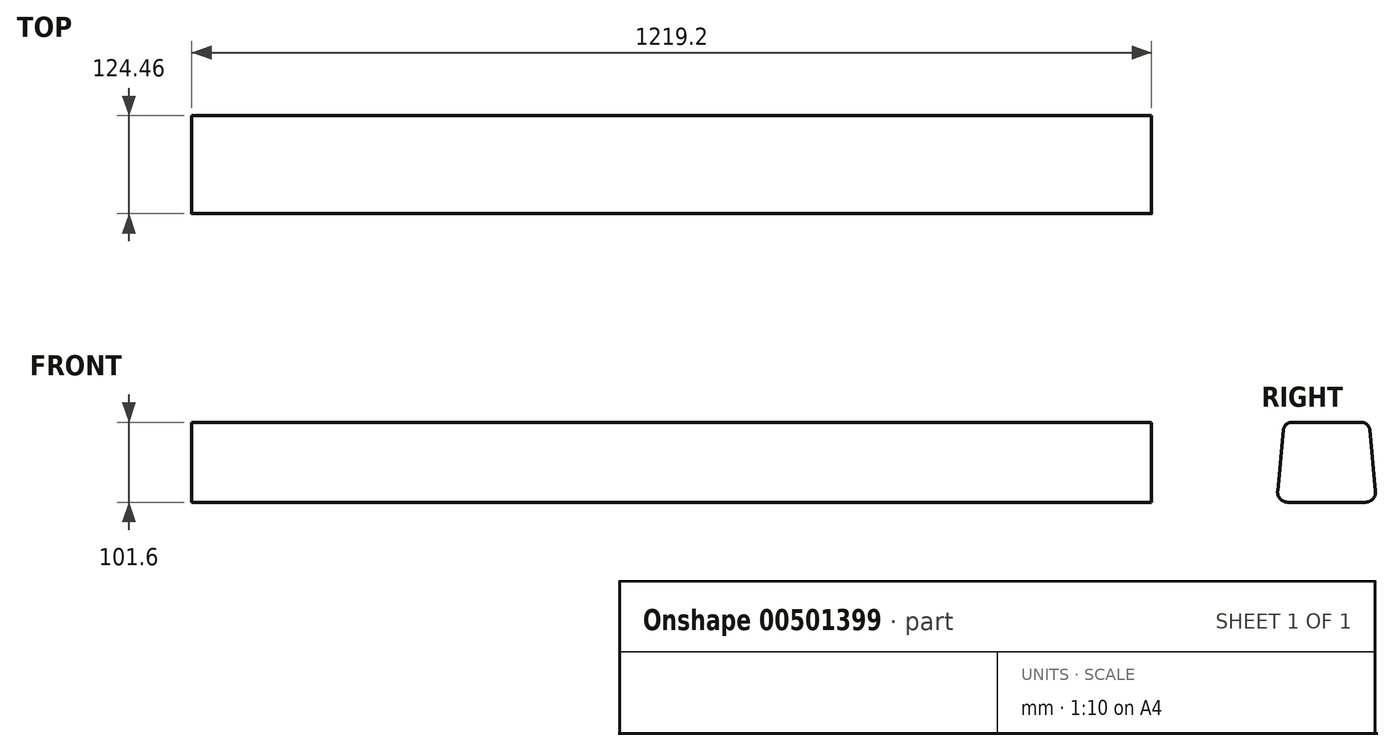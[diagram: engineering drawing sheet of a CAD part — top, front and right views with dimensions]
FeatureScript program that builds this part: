
annotation { "Feature Type Name" : "Feature", "Feature Type Description" : "" }
export const myFeature = defineFeature(function(context is Context, id is Id, definition is map)
    precondition{}
    {
        {
            var Q0;
            Q0=qCreatedBy(makeId("Top.planeOp"),FACE);
            var sketch = newSketch(context, id + "F0", { "sketchPlane" : qUnion([Q0])});
            skLineSegment(sketch, "E0.bottom", {"start": v(0, 0) * mm, "end": v(1219.2, 0) * mm});
            skLineSegment(sketch, "E0.top", {"start": v(0, 127) * mm, "end": v(1219.2, 127) * mm});
            skLineSegment(sketch, "E0.left", {"start": v(0, 0) * mm, "end": v(0, 127) * mm});
            skLineSegment(sketch, "E0.right", {"start": v(1219.2, 0) * mm, "end": v(1219.2, 127) * mm});
            skSolve(sketch);
        }
        {
            var Q0;
            Q0 = qSketchRegion(id + "F0", true);
            extrude(context, id + "F1", {"entities" : qUnion([Q0]), "depth" : 101.6 * mm});
        }
        {
            var Q0;
            Q0=makeQuery(id+"F1.opExtrude","SWEPT_FACE",FACE,{"disambiguationData":[OSD([sQuery(id+"F0.wireOp",EDGE,"E0.right")])]});
            var sketch = newSketch(context, id + "F2", { "sketchPlane" : qUnion([Q0])});
            skLineSegment(sketch, "E1", {"start": v(0, 101.6) * mm, "end": v(9.58, 101.6) * mm});
            skLineSegment(sketch, "E2", {"start": v(0, 101.6) * mm, "end": v(0, 0) * mm});
            skLineSegment(sketch, "E3", {"start": v(0, 0) * mm, "end": v(7.05, 0) * mm});
            skLineSegment(sketch, "E4", {"start": v(8.66, 91.9) * mm, "end": v(1.33, 14.1) * mm});
            skArc(sketch, "E5", {"start": v(19.33, 101.6) * mm, "mid": v(12.12, 98.81) * mm, "end": v(8.66, 91.9) * mm});
            skPoint(sketch, "E5.first.point", {"position": v(19.33, 101.6) * mm});
            skPoint(sketch, "E5.second.point", {"position": v(8.66, 91.9) * mm});
            skPoint(sketch, "E5.third.point", {"position": v(26.38, 82.84) * mm});
            skArc(sketch, "E6", {"start": v(1.33, 14.1) * mm, "mid": v(4.63, 4.21) * mm, "end": v(14.16, 0) * mm});
            skPoint(sketch, "E6.first.point", {"position": v(1.33, 14.1) * mm});
            skPoint(sketch, "E6.second.point", {"position": v(14.16, 0) * mm});
            skPoint(sketch, "E6.third.point", {"position": v(25.03, 19.8) * mm});
            skLineSegment(sketch, "E7", {"start": v(9.58, 101.6) * mm, "end": v(19.33, 101.6) * mm});
            skLineSegment(sketch, "E8", {"start": v(14.16, 0) * mm, "end": v(7.05, 0) * mm});
            skLineSegment(sketch, "E9", {"start": v(63.5, 101.6) * mm, "end": v(63.5, 0) * mm, "construction": true});
            skArc(sketch, "E10.MirrorCS", {"start": v(107.67, 101.6) * mm, "mid": v(114.88, 98.81) * mm, "end": v(118.34, 91.9) * mm});
            skLineSegment(sketch, "E11.MirrorCS", {"start": v(118.34, 91.9) * mm, "end": v(125.67, 14.1) * mm});
            skArc(sketch, "E12.MirrorCS", {"start": v(125.67, 14.1) * mm, "mid": v(122.37, 4.21) * mm, "end": v(112.84, 0) * mm});
            skLineSegment(sketch, "E13.MirrorCS", {"start": v(112.84, 0) * mm, "end": v(119.95, 0) * mm});
            skLineSegment(sketch, "E14.MirrorCS", {"start": v(127, 0) * mm, "end": v(119.95, 0) * mm});
            skLineSegment(sketch, "E15.MirrorCS", {"start": v(127, 101.6) * mm, "end": v(127, 0) * mm});
            skLineSegment(sketch, "E16.MirrorCS", {"start": v(127, 101.6) * mm, "end": v(117.42, 101.6) * mm});
            skLineSegment(sketch, "E17.MirrorCS", {"start": v(117.42, 101.6) * mm, "end": v(107.67, 101.6) * mm});
            skSolve(sketch);
        }
        {
            var Q0;
            Q0 = qSketchRegion(id + "F2", true);
            extrude(context, id + "F3", {"entities" : qUnion([Q0]), "operationType" : NewBodyOperationType.REMOVE, "endBound" : BoundingType.UP_TO_NEXT, "oppositeDirection" : true, "depth" : 25.4 * mm});
        }
    });
